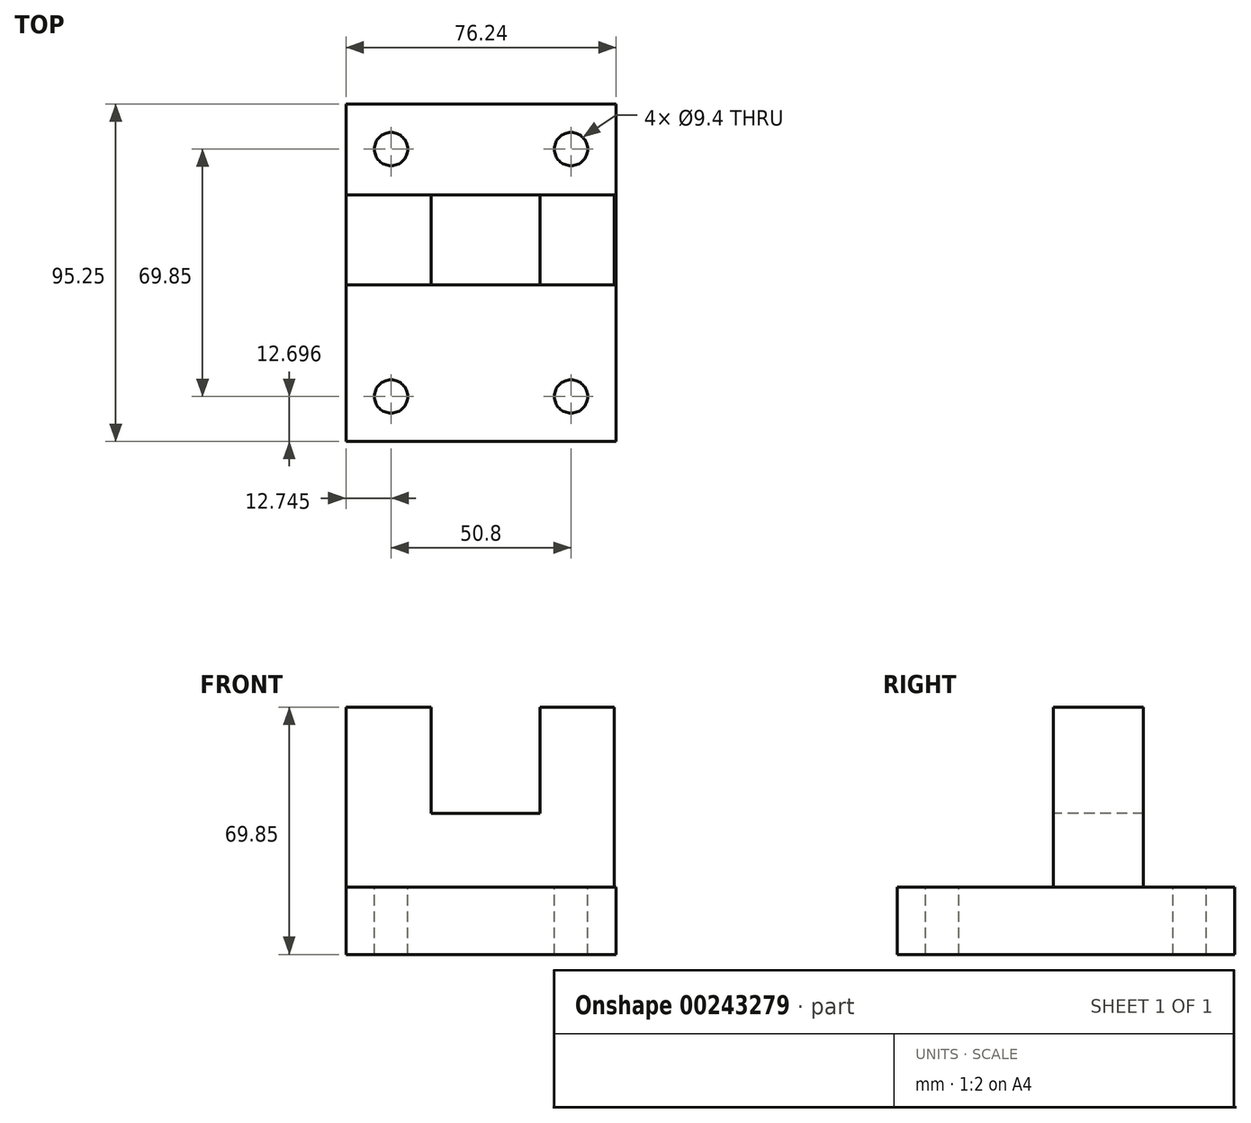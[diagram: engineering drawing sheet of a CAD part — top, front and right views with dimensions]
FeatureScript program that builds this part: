
annotation { "Feature Type Name" : "Feature", "Feature Type Description" : "" }
export const myFeature = defineFeature(function(context is Context, id is Id, definition is map)
    precondition{}
    {
        {
            var Q0;
            Q0=qCreatedBy(makeId("Top.planeOp"),FACE);
            var sketch = newSketch(context, id + "F0", { "sketchPlane" : qUnion([Q0])});
            skLineSegment(sketch, "E0.bottom", {"start": v(-24, -37.85) * mm, "end": v(52.2, -37.85) * mm});
            skLineSegment(sketch, "E0.top", {"start": v(-24, 57.4) * mm, "end": v(52.2, 57.4) * mm});
            skLineSegment(sketch, "E0.left", {"start": v(-24, -37.85) * mm, "end": v(-24, 57.4) * mm});
            skLineSegment(sketch, "E0.right", {"start": v(52.2, -37.85) * mm, "end": v(52.2, 57.4) * mm});
            skSolve(sketch);
        }
        {
            var Q0;
            Q0=makeQuery(id+"F0.imprint","IMPRINT",FACE,{"disambiguationData":[TD([[makeQuery(id+"F0.imprint","IMPRINT",EDGE,{"derivedFrom":sQuery(id+"F0.wireOp",EDGE,"E0.bottom")}),1.0]])]});
            var sketch = newSketch(context, id + "F1", { "sketchPlane" : qUnion([Q0])});
            skCircle(sketch, "E1", {"center": v(-11.3, -25.15) * mm, "radius": 4.7 * mm});
            skCircle(sketch, "E2", {"center": v(-11.3, 44.7) * mm, "radius": 4.7 * mm});
            skCircle(sketch, "E3", {"center": v(39.5, 44.7) * mm, "radius": 4.7 * mm});
            skCircle(sketch, "E4", {"center": v(39.5, -25.15) * mm, "radius": 4.7 * mm});
            skSolve(sketch);
        }
        {
            var Q0;
            Q0=makeQuery(id+"F0.imprint","IMPRINT",FACE,{"disambiguationData":[TD([[makeQuery(id+"F0.imprint","IMPRINT",EDGE,{"derivedFrom":sQuery(id+"F0.wireOp",EDGE,"E0.bottom")}),1.0]])]});
            var sketch = newSketch(context, id + "F2", { "sketchPlane" : qUnion([Q0])});
            skLineSegment(sketch, "E5.bottom", {"start": v(-24.04, 31.7) * mm, "end": v(51.7, 31.7) * mm});
            skLineSegment(sketch, "E5.top", {"start": v(-24.04, 6.3) * mm, "end": v(51.7, 6.3) * mm});
            skLineSegment(sketch, "E5.left", {"start": v(-24.04, 31.7) * mm, "end": v(-24.04, 6.3) * mm});
            skLineSegment(sketch, "E5.right", {"start": v(51.7, 31.7) * mm, "end": v(51.7, 6.3) * mm});
            skSolve(sketch);
        }
        {
            var Q0;
            {var subQ0=sQuery(id+"F2.wireOp",EDGE,"E5.left");Q0=makeQuery(id+"F2.imprint","IMPRINT",FACE,{"disambiguationData":[TD([[makeQuery(id+"F2.imprint","IMPRINT",EDGE,{"derivedFrom":subQ0}),1.0]])]});}
            var Q1;
            {var subQ0=sQuery(id+"F2.wireOp",EDGE,"E5.right");Q1=makeQuery(id+"F2.imprint","IMPRINT",FACE,{"disambiguationData":[TD([[makeQuery(id+"F2.imprint","IMPRINT",EDGE,{"derivedFrom":subQ0}),-1.0]])]});}
            extrude(context, id + "F3", {"entities" : qUnion([Q0, Q1]), "depth" : 50.8 * mm});
        }
        {
            var Q0;
            Q0=makeQuery(id+"F1.imprint","IMPRINT",FACE,{"disambiguationData":[TD([[makeQuery(id+"F1.imprint","IMPRINT",EDGE,{"derivedFrom":sQuery(id+"F1.wireOp",EDGE,"E1")}),-1.0]])]});
            extrude(context, id + "F4", {"entities" : qUnion([Q0]), "operationType" : NewBodyOperationType.ADD, "oppositeDirection" : true, "depth" : 19.05 * mm});
        }
        {
            var Q0;
            Q0=makeQuery(id+"F3.opExtrude","SWEPT_FACE",FACE,{"disambiguationData":[OSD([sQuery(id+"F2.wireOp",EDGE,"E5.top")])]});
            var sketch = newSketch(context, id + "F5", { "sketchPlane" : qUnion([Q0])});
            skLineSegment(sketch, "E6.bottom", {"start": v(0, 50.8) * mm, "end": v(30.75, 50.8) * mm});
            skLineSegment(sketch, "E6.top", {"start": v(0, 20.81) * mm, "end": v(30.75, 20.81) * mm});
            skLineSegment(sketch, "E6.left", {"start": v(0, 50.8) * mm, "end": v(0, 20.81) * mm});
            skLineSegment(sketch, "E6.right", {"start": v(30.75, 50.8) * mm, "end": v(30.75, 20.81) * mm});
            skSolve(sketch);
        }
        {
            var Q0;
            Q0 = qSketchRegion(id + "F5", true);
            extrude(context, id + "F6", {"entities" : qUnion([Q0]), "operationType" : NewBodyOperationType.REMOVE, "oppositeDirection" : true, "depth" : 31.75 * mm});
        }
    });
